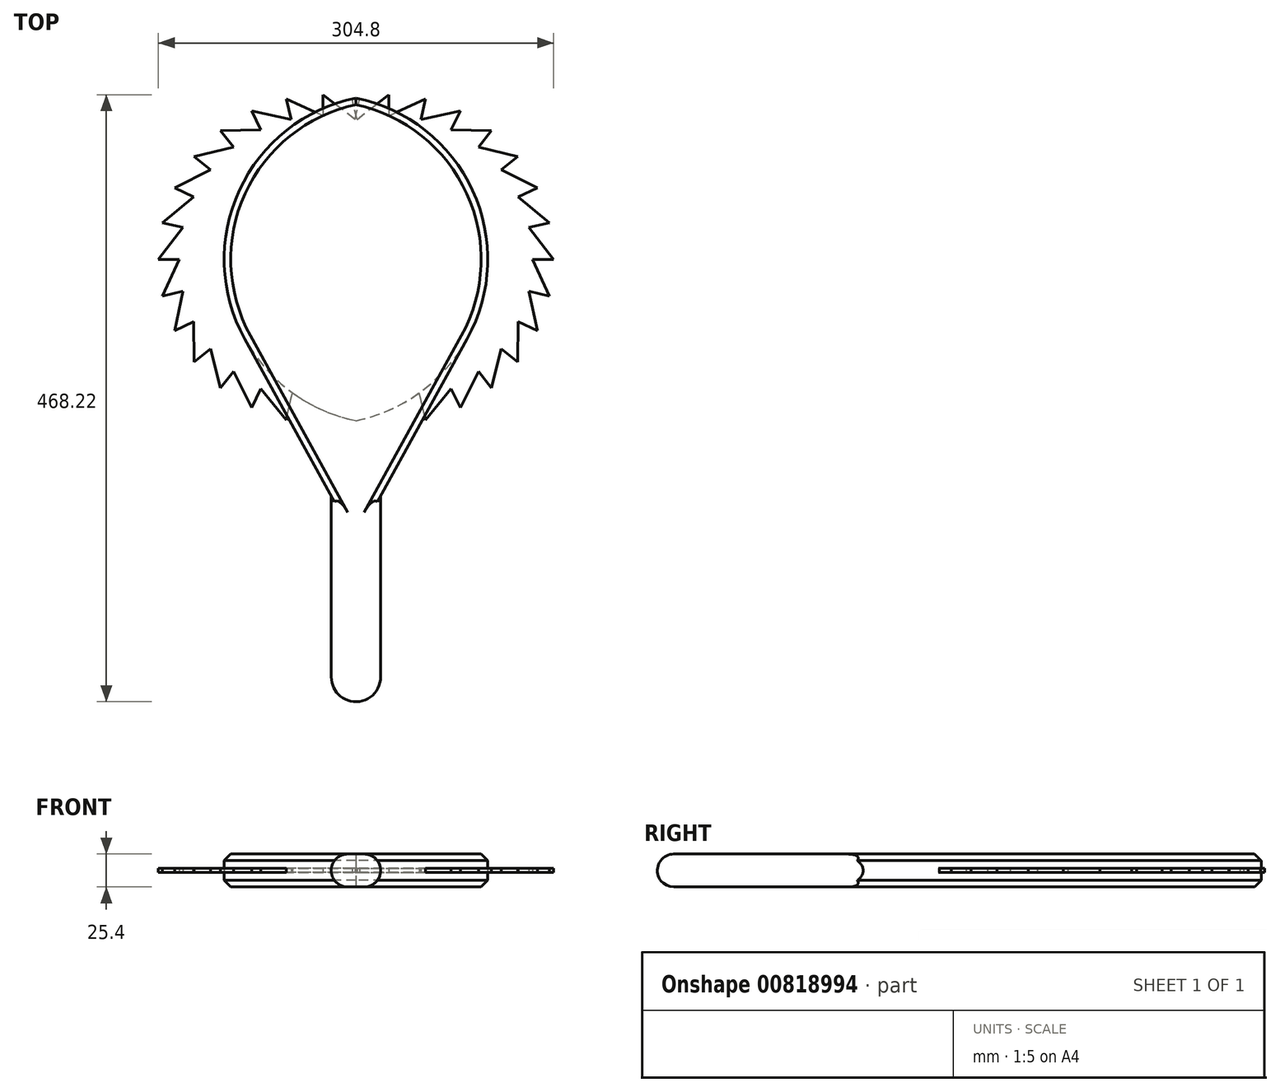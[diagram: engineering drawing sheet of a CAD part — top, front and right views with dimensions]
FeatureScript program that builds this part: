
annotation { "Feature Type Name" : "Feature", "Feature Type Description" : "" }
export const myFeature = defineFeature(function(context is Context, id is Id, definition is map)
    precondition{}
    {
        {
            var Q0;
            Q0=qCreatedBy(makeId("Top.planeOp"),FACE);
            var sketch = newSketch(context, id + "F0", { "sketchPlane" : qUnion([Q0])});
            skCircle(sketch, "E0", {"center": v(-25.4, 0) * mm, "radius": 127 * mm});
            skCircle(sketch, "E1", {"center": v(25.4, 0) * mm, "radius": 127 * mm});
            skLineSegment(sketch, "E2", {"start": v(-25.4, 0) * mm, "end": v(25.4, 0) * mm, "construction": true});
            skLineSegment(sketch, "E3", {"start": v(-25.4, 127) * mm, "end": v(25.4, 127) * mm, "construction": true});
            skLineSegment(sketch, "E4", {"start": v(-19.05, -118.97) * mm, "end": v(-19.05, -322.17) * mm});
            skLineSegment(sketch, "E5", {"start": v(19.05, -118.97) * mm, "end": v(19.05, -322.17) * mm});
            skArc(sketch, "E6", {"start": v(-19.05, -322.17) * mm, "mid": v(0, -341.22) * mm, "end": v(19.05, -322.17) * mm});
            skPoint(sketch, "E7.0.internal.orphan", {"position": v(-101.6, 0) * mm});
            skLineSegment(sketch, "E8", {"start": v(-85.83, -61.3) * mm, "end": v(-19.05, -182.47) * mm});
            skLineSegment(sketch, "E9", {"start": v(85.83, -61.3) * mm, "end": v(19.05, -182.47) * mm});
            skLineSegment(sketch, "E10", {"start": v(73.45, 99.77) * mm, "end": v(80.5, 114.42) * mm});
            skLineSegment(sketch, "E11", {"start": v(94.44, 86.58) * mm, "end": v(104.58, 99.3) * mm});
            skLineSegment(sketch, "E12", {"start": v(111.98, 69.04) * mm, "end": v(124.7, 79.18) * mm});
            skLineSegment(sketch, "E13", {"start": v(125.17, 48.05) * mm, "end": v(139.82, 55.1) * mm});
            skLineSegment(sketch, "E14", {"start": v(133.36, 24.64) * mm, "end": v(149.22, 28.26) * mm});
            skLineSegment(sketch, "E15", {"start": v(136.14, 0) * mm, "end": v(152.4, 0) * mm});
            skLineSegment(sketch, "E16", {"start": v(133.36, -24.64) * mm, "end": v(149.22, -28.26) * mm});
            skLineSegment(sketch, "E17", {"start": v(125.17, -48.05) * mm, "end": v(139.82, -55.1) * mm});
            skLineSegment(sketch, "E18", {"start": v(111.98, -69.04) * mm, "end": v(124.7, -79.18) * mm});
            skLineSegment(sketch, "E19", {"start": v(53.66, 123.82) * mm, "end": v(50.04, 107.96) * mm});
            skLineSegment(sketch, "E20", {"start": v(25.4, 127) * mm, "end": v(25.4, 110.74) * mm});
            skLineSegment(sketch, "E21", {"start": v(104.58, -99.3) * mm, "end": v(94.44, -86.58) * mm});
            skLineSegment(sketch, "E22", {"start": v(80.5, -114.42) * mm, "end": v(73.45, -99.77) * mm});
            skLineSegment(sketch, "E23", {"start": v(53.66, -123.82) * mm, "end": v(48.9, -103) * mm});
            skLineSegment(sketch, "E24", {"start": v(53.66, -123.82) * mm, "end": v(73.45, -99.77) * mm});
            skLineSegment(sketch, "E25", {"start": v(53.66, -123.82) * mm, "end": v(80.5, -114.42) * mm, "construction": true});
            skLineSegment(sketch, "E26", {"start": v(94.44, -86.58) * mm, "end": v(80.5, -114.42) * mm});
            skLineSegment(sketch, "E27", {"start": v(111.98, -69.04) * mm, "end": v(104.58, -99.3) * mm});
            skLineSegment(sketch, "E28", {"start": v(125.17, -48.05) * mm, "end": v(124.7, -79.18) * mm});
            skLineSegment(sketch, "E29", {"start": v(133.36, -24.64) * mm, "end": v(139.82, -55.1) * mm});
            skLineSegment(sketch, "E30", {"start": v(136.14, 0) * mm, "end": v(149.22, -28.26) * mm});
            skLineSegment(sketch, "E31", {"start": v(133.36, 24.64) * mm, "end": v(152.4, 0) * mm});
            skLineSegment(sketch, "E32", {"start": v(125.17, 48.05) * mm, "end": v(149.22, 28.26) * mm});
            skLineSegment(sketch, "E33", {"start": v(111.98, 69.04) * mm, "end": v(139.82, 55.1) * mm});
            skLineSegment(sketch, "E34", {"start": v(73.45, 99.77) * mm, "end": v(104.58, 99.3) * mm});
            skLineSegment(sketch, "E35", {"start": v(50.04, 107.96) * mm, "end": v(80.5, 114.42) * mm});
            skLineSegment(sketch, "E36", {"start": v(25.4, 110.74) * mm, "end": v(53.66, 123.82) * mm});
            skLineSegment(sketch, "E37", {"start": v(0.76, 107.96) * mm, "end": v(-2.86, 123.82) * mm});
            skLineSegment(sketch, "E38", {"start": v(0.76, 107.96) * mm, "end": v(25.4, 127) * mm});
            skLineSegment(sketch, "E39", {"start": v(94.44, 86.58) * mm, "end": v(124.7, 79.18) * mm});
            skLineSegment(sketch, "E40.trimOffspring", {"start": v(69.33, -91.23) * mm, "end": v(67.24, -86.87) * mm, "construction": true});
            skLineSegment(sketch, "E41.trimOffspring", {"start": v(81.11, -69.86) * mm, "end": v(80.86, -69.55) * mm, "construction": true});
            skSolve(sketch);
        }
        {
            var Q0;
            {var subQ2=sQuery(id+"F0.wireOp",EDGE,"E0");var subQ5=makeQuery(id+"F0.imprint","INTERSECT",VERTEX,{"derivedFrom":[subQ2,sQuery(id+"F0.wireOp",EDGE,"E5")]});Q0=makeQuery(id+"F0.imprint","IMPRINT",FACE,{"disambiguationData":[TD([[makeQuery(id+"F0.imprint","IMPRINT",EDGE,{"disambiguationData":[TD([[subQ5,1.0]])],"derivedFrom":subQ2}),1.0]])]});}
            var Q1;
            {var subQ0=sQuery(id+"F0.wireOp",EDGE,"E9");var subQ1=sQuery(id+"F0.wireOp",EDGE,"E1");var subQ2=makeQuery(id+"F0.imprint","INTERSECT",VERTEX,{"derivedFrom":[subQ1,subQ0]});Q1=makeQuery(id+"F0.imprint","IMPRINT",FACE,{"disambiguationData":[TD([[makeQuery(id+"F0.imprint","IMPRINT",EDGE,{"disambiguationData":[TD([[subQ2,1.0]])],"derivedFrom":subQ1}),-1.0]])]});}
            var Q2;
            {var subQ0=sQuery(id+"F0.wireOp",EDGE,"E5");var subQ1=sQuery(id+"F0.wireOp",EDGE,"E0");var subQ2=makeQuery(id+"F0.imprint","INTERSECT",VERTEX,{"derivedFrom":[subQ1,subQ0]});Q2=makeQuery(id+"F0.imprint","IMPRINT",FACE,{"disambiguationData":[TD([[makeQuery(id+"F0.imprint","IMPRINT",EDGE,{"disambiguationData":[TD([[subQ2,1.0]])],"derivedFrom":subQ1}),-1.0]])]});}
            var Q3;
            {var subQ0=sQuery(id+"F0.wireOp",EDGE,"E8");var subQ1=sQuery(id+"F0.wireOp",EDGE,"E0");var subQ2=makeQuery(id+"F0.imprint","INTERSECT",VERTEX,{"derivedFrom":[subQ1,subQ0]});Q3=makeQuery(id+"F0.imprint","IMPRINT",FACE,{"disambiguationData":[TD([[makeQuery(id+"F0.imprint","IMPRINT",EDGE,{"disambiguationData":[TD([[subQ2,-1.0]])],"derivedFrom":subQ1}),1.0]])]});}
            var Q4;
            {var subQ0=sQuery(id+"F0.wireOp",EDGE,"E5");var subQ1=sQuery(id+"F0.wireOp",EDGE,"E0");var subQ2=makeQuery(id+"F0.imprint","INTERSECT",VERTEX,{"derivedFrom":[subQ1,subQ0]});Q4=makeQuery(id+"F0.imprint","IMPRINT",FACE,{"disambiguationData":[TD([[makeQuery(id+"F0.imprint","IMPRINT",EDGE,{"disambiguationData":[TD([[subQ2,-1.0]])],"derivedFrom":subQ1}),-1.0]])]});}
            var Q5;
            {var subQ6=sQuery(id+"F0.wireOp",EDGE,"E6");Q5=makeQuery(id+"F0.imprint","IMPRINT",FACE,{"disambiguationData":[TD([[makeQuery(id+"F0.imprint","IMPRINT",EDGE,{"derivedFrom":subQ6}),1.0]])]});}
            var Q6;
            {var subQ0=sQuery(id+"F0.wireOp",EDGE,"E8");var subQ1=sQuery(id+"F0.wireOp",EDGE,"E0");var subQ2=makeQuery(id+"F0.imprint","INTERSECT",VERTEX,{"derivedFrom":[subQ1,subQ0]});Q6=makeQuery(id+"F0.imprint","IMPRINT",FACE,{"disambiguationData":[TD([[makeQuery(id+"F0.imprint","IMPRINT",EDGE,{"disambiguationData":[TD([[subQ2,-1.0]])],"derivedFrom":subQ1}),-1.0]])]});}
            var Q7;
            {var subQ0=sQuery(id+"F0.wireOp",EDGE,"E4");var subQ1=sQuery(id+"F0.wireOp",EDGE,"E0");var subQ2=makeQuery(id+"F0.imprint","INTERSECT",VERTEX,{"derivedFrom":[subQ1,subQ0]});Q7=makeQuery(id+"F0.imprint","IMPRINT",FACE,{"disambiguationData":[TD([[makeQuery(id+"F0.imprint","IMPRINT",EDGE,{"disambiguationData":[TD([[subQ2,-1.0]])],"derivedFrom":subQ1}),1.0]])]});}
            var Q8;
            {var subQ0=sQuery(id+"F0.wireOp",EDGE,"E9");var subQ1=sQuery(id+"F0.wireOp",EDGE,"E0");var subQ2=makeQuery(id+"F0.imprint","INTERSECT",VERTEX,{"derivedFrom":[subQ1,subQ0]});Q8=makeQuery(id+"F0.imprint","IMPRINT",FACE,{"disambiguationData":[TD([[makeQuery(id+"F0.imprint","IMPRINT",EDGE,{"disambiguationData":[TD([[subQ2,1.0]])],"derivedFrom":subQ1}),-1.0]])]});}
            var Q9;
            {var subQ5=sQuery(id+"F0.wireOp",EDGE,"E37");Q9=makeQuery(id+"F0.imprint","IMPRINT",FACE,{"disambiguationData":[TD([[makeQuery(id+"F0.imprint","IMPRINT",EDGE,{"derivedFrom":subQ5}),-1.0]])]});}
            var Q10;
            {var subQ0=sQuery(id+"F0.wireOp",EDGE,"E20");var subQ1=sQuery(id+"F0.wireOp",EDGE,"E0");var subQ2=makeQuery(id+"F0.imprint","INTERSECT",VERTEX,{"derivedFrom":[subQ1,subQ0]});Q10=makeQuery(id+"F0.imprint","IMPRINT",FACE,{"disambiguationData":[TD([[makeQuery(id+"F0.imprint","IMPRINT",EDGE,{"disambiguationData":[TD([[subQ2,1.0]])],"derivedFrom":subQ1}),1.0]])]});}
            extrude(context, id + "F1", {"entities" : qUnion([Q0, Q1, Q2, Q3, Q4, Q5, Q6, Q7, Q8, Q9, Q10]), "depth" : 12.7 * mm, "offsetDistance" : 25.4 * mm, "hasSecondDirection" : true, "secondDirectionOppositeDirection" : true, "secondDirectionDepth" : 12.7 * mm});
        }
        {
            var Q0;
            Q0=makeQuery(id+"F0.imprint","IMPRINT",FACE,{"disambiguationData":[TD([[makeQuery(id+"F0.imprint","IMPRINT",EDGE,{"derivedFrom":sQuery(id+"F0.wireOp",EDGE,"E10")}),1.0]])]});
            var Q1;
            {var subQ0=sQuery(id+"F0.wireOp",EDGE,"E20");var subQ1=sQuery(id+"F0.wireOp",EDGE,"E0");var subQ2=makeQuery(id+"F0.imprint","INTERSECT",VERTEX,{"derivedFrom":[subQ1,subQ0]});Q1=makeQuery(id+"F0.imprint","IMPRINT",FACE,{"disambiguationData":[TD([[makeQuery(id+"F0.imprint","IMPRINT",EDGE,{"disambiguationData":[TD([[subQ2,-1.0]])],"derivedFrom":subQ1}),-1.0]])]});}
            var Q2;
            {var subQ15=sQuery(id+"F0.wireOp",EDGE,"E37");Q2=makeQuery(id+"F0.imprint","IMPRINT",FACE,{"disambiguationData":[TD([[makeQuery(id+"F0.imprint","IMPRINT",EDGE,{"derivedFrom":subQ15}),1.0]])]});}
            var Q3;
            {var subQ0=sQuery(id+"F0.wireOp",EDGE,"E9");var subQ1=sQuery(id+"F0.wireOp",EDGE,"E0");var subQ2=makeQuery(id+"F0.imprint","INTERSECT",VERTEX,{"derivedFrom":[subQ1,subQ0]});Q3=makeQuery(id+"F0.imprint","IMPRINT",FACE,{"disambiguationData":[TD([[makeQuery(id+"F0.imprint","IMPRINT",EDGE,{"disambiguationData":[TD([[subQ2,1.0]])],"derivedFrom":subQ1}),-1.0]])]});}
            extrude(context, id + "F2", {"entities" : qUnion([Q0, Q1, Q2, Q3]), "depth" : 1.59 * mm, "offsetDistance" : 25.4 * mm, "hasSecondDirection" : true, "secondDirectionOppositeDirection" : true, "secondDirectionDepth" : 1.59 * mm});
        }
        {
            var Q0;
            Q0=makeQuery(id+"F2.opExtrude","SWEPT_BODY",BODY,{"disambiguationData":[OSD([sQuery(id+"F0.wireOp",EDGE,"E0"),sQuery(id+"F0.wireOp",EDGE,"E1"),sQuery(id+"F0.wireOp",EDGE,"E10"),sQuery(id+"F0.wireOp",EDGE,"E11"),sQuery(id+"F0.wireOp",EDGE,"E12"),sQuery(id+"F0.wireOp",EDGE,"E13"),sQuery(id+"F0.wireOp",EDGE,"E14"),sQuery(id+"F0.wireOp",EDGE,"E15"),sQuery(id+"F0.wireOp",EDGE,"E16"),sQuery(id+"F0.wireOp",EDGE,"E17"),sQuery(id+"F0.wireOp",EDGE,"E18"),sQuery(id+"F0.wireOp",EDGE,"E19"),sQuery(id+"F0.wireOp",EDGE,"E20"),sQuery(id+"F0.wireOp",EDGE,"E21"),sQuery(id+"F0.wireOp",EDGE,"E22"),sQuery(id+"F0.wireOp",EDGE,"E23"),sQuery(id+"F0.wireOp",EDGE,"E24"),sQuery(id+"F0.wireOp",EDGE,"E26"),sQuery(id+"F0.wireOp",EDGE,"E27"),sQuery(id+"F0.wireOp",EDGE,"E28"),sQuery(id+"F0.wireOp",EDGE,"E29"),sQuery(id+"F0.wireOp",EDGE,"E30"),sQuery(id+"F0.wireOp",EDGE,"E31"),sQuery(id+"F0.wireOp",EDGE,"E32"),sQuery(id+"F0.wireOp",EDGE,"E33"),sQuery(id+"F0.wireOp",EDGE,"E34"),sQuery(id+"F0.wireOp",EDGE,"E35"),sQuery(id+"F0.wireOp",EDGE,"E36"),sQuery(id+"F0.wireOp",EDGE,"E37"),sQuery(id+"F0.wireOp",EDGE,"E38"),sQuery(id+"F0.wireOp",EDGE,"E39")])]});
            var Q1;
            Q1=qCreatedBy(makeId("Right.planeOp"),FACE);
            mirror(context, id + "F3", {"entities" : qUnion([Q0]), "mirrorPlane" : qUnion([Q1])});
        }
        {
            var Q0;
            Q0=makeQuery(id+"F1.opExtrude","CAP_EDGE",EDGE,{"disambiguationData":[OSD([sQuery(id+"F0.wireOp",EDGE,"E9")])],"isStart":true});
            var Q1;
            Q1=makeQuery(id+"F1.opExtrude","CAP_EDGE",EDGE,{"disambiguationData":[OSD([sQuery(id+"F0.wireOp",EDGE,"E0")])],"isStart":true});
            var Q2;
            Q2=makeQuery(id+"F1.opExtrude","CAP_EDGE",EDGE,{"disambiguationData":[OSD([sQuery(id+"F0.wireOp",EDGE,"E8")])],"isStart":true});
            var Q3;
            Q3=makeQuery(id+"F1.opExtrude","CAP_EDGE",EDGE,{"disambiguationData":[OSD([sQuery(id+"F0.wireOp",EDGE,"E1")])],"isStart":true});
            var Q4;
            Q4=makeQuery(id+"F1.opExtrude","CAP_EDGE",EDGE,{"disambiguationData":[OSD([sQuery(id+"F0.wireOp",EDGE,"E8")])],"isStart":false});
            var Q5;
            Q5=makeQuery(id+"F1.opExtrude","CAP_EDGE",EDGE,{"disambiguationData":[OSD([sQuery(id+"F0.wireOp",EDGE,"E1")])],"isStart":false});
            var Q6;
            Q6=makeQuery(id+"F1.opExtrude","CAP_EDGE",EDGE,{"disambiguationData":[OSD([sQuery(id+"F0.wireOp",EDGE,"E9")])],"isStart":false});
            var Q7;
            Q7=makeQuery(id+"F1.opExtrude","CAP_EDGE",EDGE,{"disambiguationData":[OSD([sQuery(id+"F0.wireOp",EDGE,"E0")])],"isStart":false});
            chamfer(context, id + "F4", {"entities" : qUnion([Q0, Q1, Q2, Q3, Q4, Q5, Q6, Q7]), "width" : 5.08 * mm, "tangentPropagation" : true});
        }
        {
            var Q0;
            Q0=makeQuery(id+"F1.opExtrude","CAP_EDGE",EDGE,{"disambiguationData":[OSD([sQuery(id+"F0.wireOp",EDGE,"E5")])],"isStart":false});
            var Q1;
            Q1=makeQuery(id+"F1.opExtrude","CAP_EDGE",EDGE,{"disambiguationData":[OSD([sQuery(id+"F0.wireOp",EDGE,"E4")])],"isStart":false});
            var Q2;
            Q2=makeQuery(id+"F1.opExtrude","CAP_EDGE",EDGE,{"disambiguationData":[OSD([sQuery(id+"F0.wireOp",EDGE,"E5")])],"isStart":true});
            var Q3;
            Q3=makeQuery(id+"F1.opExtrude","CAP_EDGE",EDGE,{"disambiguationData":[OSD([sQuery(id+"F0.wireOp",EDGE,"E4")])],"isStart":true});
            var Q4;
            Q4=makeQuery(id+"F1.opExtrude","CAP_EDGE",EDGE,{"disambiguationData":[OSD([sQuery(id+"F0.wireOp",EDGE,"E6")])],"isStart":true});
            var Q5;
            Q5=makeQuery(id+"F1.opExtrude","CAP_EDGE",EDGE,{"disambiguationData":[OSD([sQuery(id+"F0.wireOp",EDGE,"E6")])],"isStart":false});
            fillet(context, id + "F5", {"entities" : qUnion([Q0, Q1, Q2, Q3, Q4, Q5]), "radius" : 12.7 * mm, "tangentPropagation" : true, "allowEdgeOverflow" : false});
        }
    });
